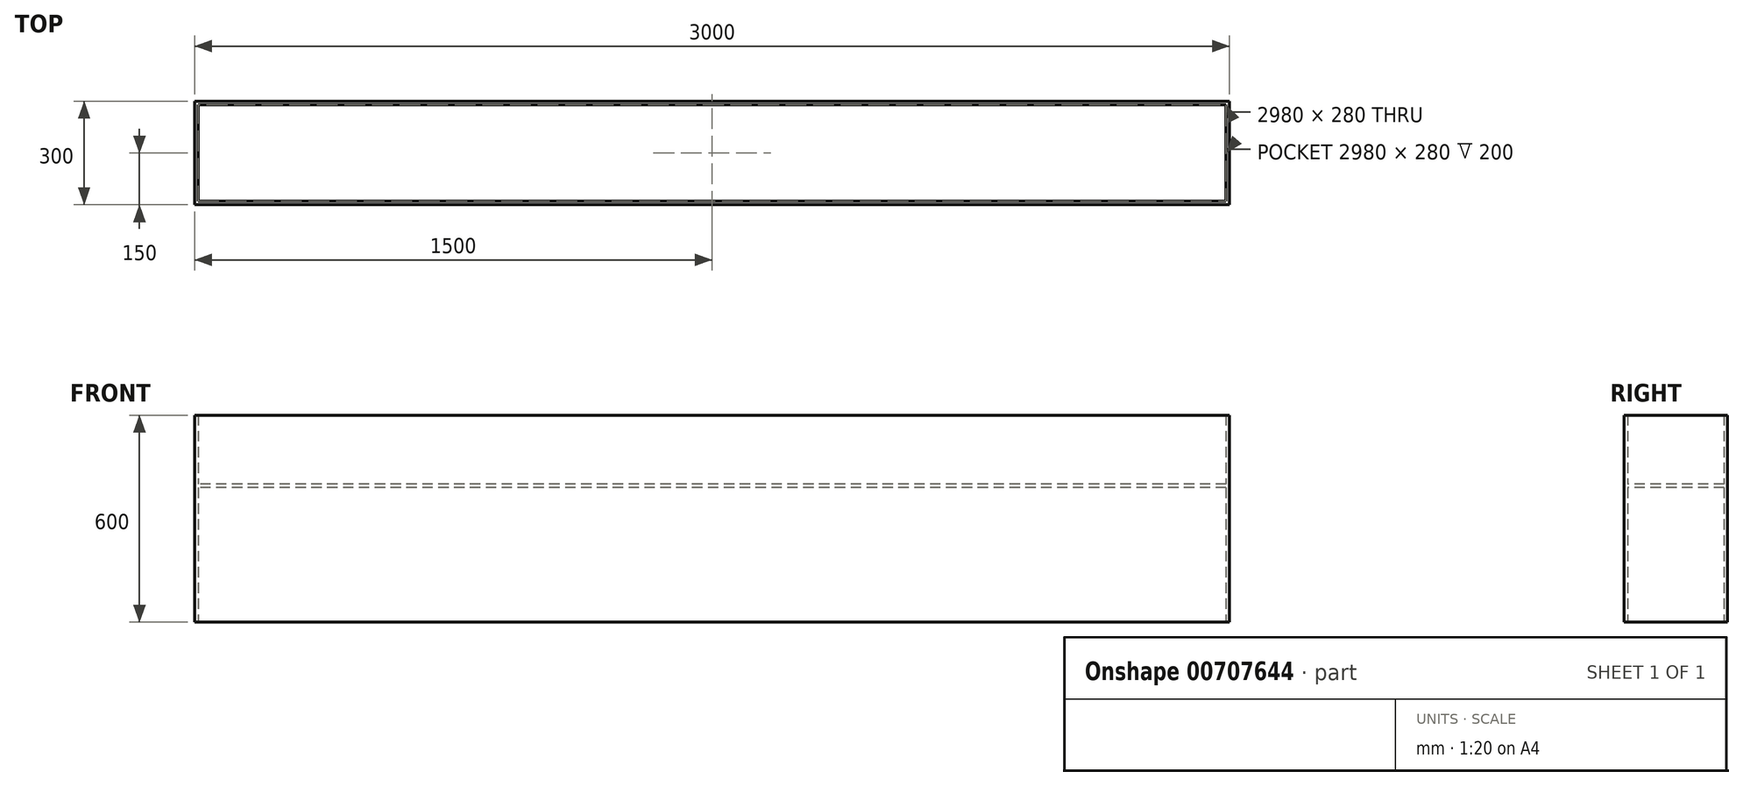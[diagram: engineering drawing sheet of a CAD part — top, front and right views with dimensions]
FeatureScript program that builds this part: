
annotation { "Feature Type Name" : "Feature", "Feature Type Description" : "" }
export const myFeature = defineFeature(function(context is Context, id is Id, definition is map)
    precondition{}
    {
        {
            var Q0;
            Q0=qCreatedBy(makeId("Top.planeOp"),FACE);
            var sketch = newSketch(context, id + "F0", { "sketchPlane" : qUnion([Q0])});
            skLineSegment(sketch, "E0.bottom", {"start": v(1500, 150) * mm, "end": v(-1500, 150) * mm});
            skLineSegment(sketch, "E0.top", {"start": v(1500, -150) * mm, "end": v(-1500, -150) * mm});
            skLineSegment(sketch, "E0.left", {"start": v(1500, 150) * mm, "end": v(1500, -150) * mm});
            skLineSegment(sketch, "E0.right", {"start": v(-1500, 150) * mm, "end": v(-1500, -150) * mm});
            skPoint(sketch, "E0.middle", {"position": v(0, 0) * mm});
            skSolve(sketch);
        }
        {
            var Q0;
            Q0=makeQuery(id+"F0.imprint","IMPRINT",FACE,{"disambiguationData":[TD([[makeQuery(id+"F0.imprint","IMPRINT",EDGE,{"derivedFrom":sQuery(id+"F0.wireOp",EDGE,"E0.bottom")}),1.0]])]});
            extrude(context, id + "F1", {"entities" : qUnion([Q0]), "depth" : 600 * mm, "offsetDistance" : 25 * mm});
        }
        {
            var Q0;
            Q0=makeQuery(id+"F1.opExtrude","CAP_FACE",FACE,{"disambiguationData":[OSD([sQuery(id+"F0.wireOp",EDGE,"E0.bottom"),sQuery(id+"F0.wireOp",EDGE,"E0.top"),sQuery(id+"F0.wireOp",EDGE,"E0.left"),sQuery(id+"F0.wireOp",EDGE,"E0.right")])],"isStart":false});
            var Q1;
            Q1=makeQuery(id+"F1.opExtrude","CAP_FACE",FACE,{"disambiguationData":[OSD([sQuery(id+"F0.wireOp",EDGE,"E0.bottom"),sQuery(id+"F0.wireOp",EDGE,"E0.top"),sQuery(id+"F0.wireOp",EDGE,"E0.left"),sQuery(id+"F0.wireOp",EDGE,"E0.right")])],"isStart":true});
            shell(context, id + "F2", {"entities" : qUnion([Q0, Q1]), "thickness" : 10 * mm});
        }
        {
            var Q0;
            Q0=makeQuery(id+"F1.opExtrude","CAP_FACE",FACE,{"disambiguationData":[OSD([sQuery(id+"F0.wireOp",EDGE,"E0.bottom"),sQuery(id+"F0.wireOp",EDGE,"E0.top"),sQuery(id+"F0.wireOp",EDGE,"E0.left"),sQuery(id+"F0.wireOp",EDGE,"E0.right")])],"isStart":true});
            cPlane(context, id + "F3", {"entities" : qUnion([Q0]), "cplaneType" : CPlaneType.OFFSET, "offset" : 400 * mm, "oppositeDirection" : true, "width" : 150 * mm, "height" : 150 * mm});
        }
        {
            var Q0;
            Q0=qCreatedBy(id+"F3.planeOp",FACE);
            var sketch = newSketch(context, id + "F4", { "sketchPlane" : qUnion([Q0])});
            skLineSegment(sketch, "E1.0", {"start": v(1490, 140) * mm, "end": v(-1490, 140) * mm});
            skLineSegment(sketch, "E2.0", {"start": v(-1490, -140) * mm, "end": v(-1490, 140) * mm});
            skLineSegment(sketch, "E3.0", {"start": v(1490, -140) * mm, "end": v(-1490, -140) * mm});
            skLineSegment(sketch, "E4.0", {"start": v(1490, -140) * mm, "end": v(1490, 140) * mm});
            skSolve(sketch);
        }
        {
            var Q0;
            Q0=makeQuery(id+"F4.imprint","IMPRINT",FACE,{"disambiguationData":[TD([[makeQuery(id+"F4.imprint","IMPRINT",EDGE,{"derivedFrom":sQuery(id+"F4.wireOp",EDGE,"E1.0")}),1.0]])]});
            extrude(context, id + "F5", {"entities" : qUnion([Q0]), "operationType" : NewBodyOperationType.ADD, "depth" : 10 * mm, "offsetDistance" : 25 * mm});
        }
    });
